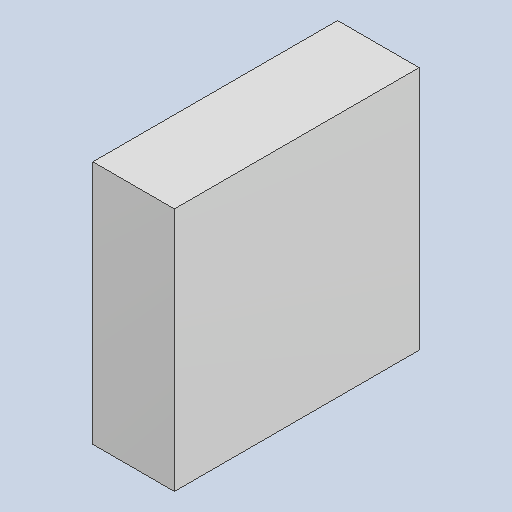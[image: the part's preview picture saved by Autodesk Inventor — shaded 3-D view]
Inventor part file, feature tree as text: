
AUTODESK INVENTOR PART (.ipt)
format: ipt  version: 2023.4 (Build 274418000, 418)  size: 81,408 bytes
history: native  units: mm
features: extrude x1
ambient origin geometry x8: Origin, YZ Plane, XZ Plane, XY Plane, X Axis, Y Axis, Z Axis, Center Point
bodies: Solid1 (feature_tree)
feature tree (1):
  extrude  "Extruded_28"  [1 undecoded]
note: 1 required parameter value undecoded (feature->parameter linkage not recoverable at this tier; creation-order binding heuristic only, values carry confidence <= 0.55)
